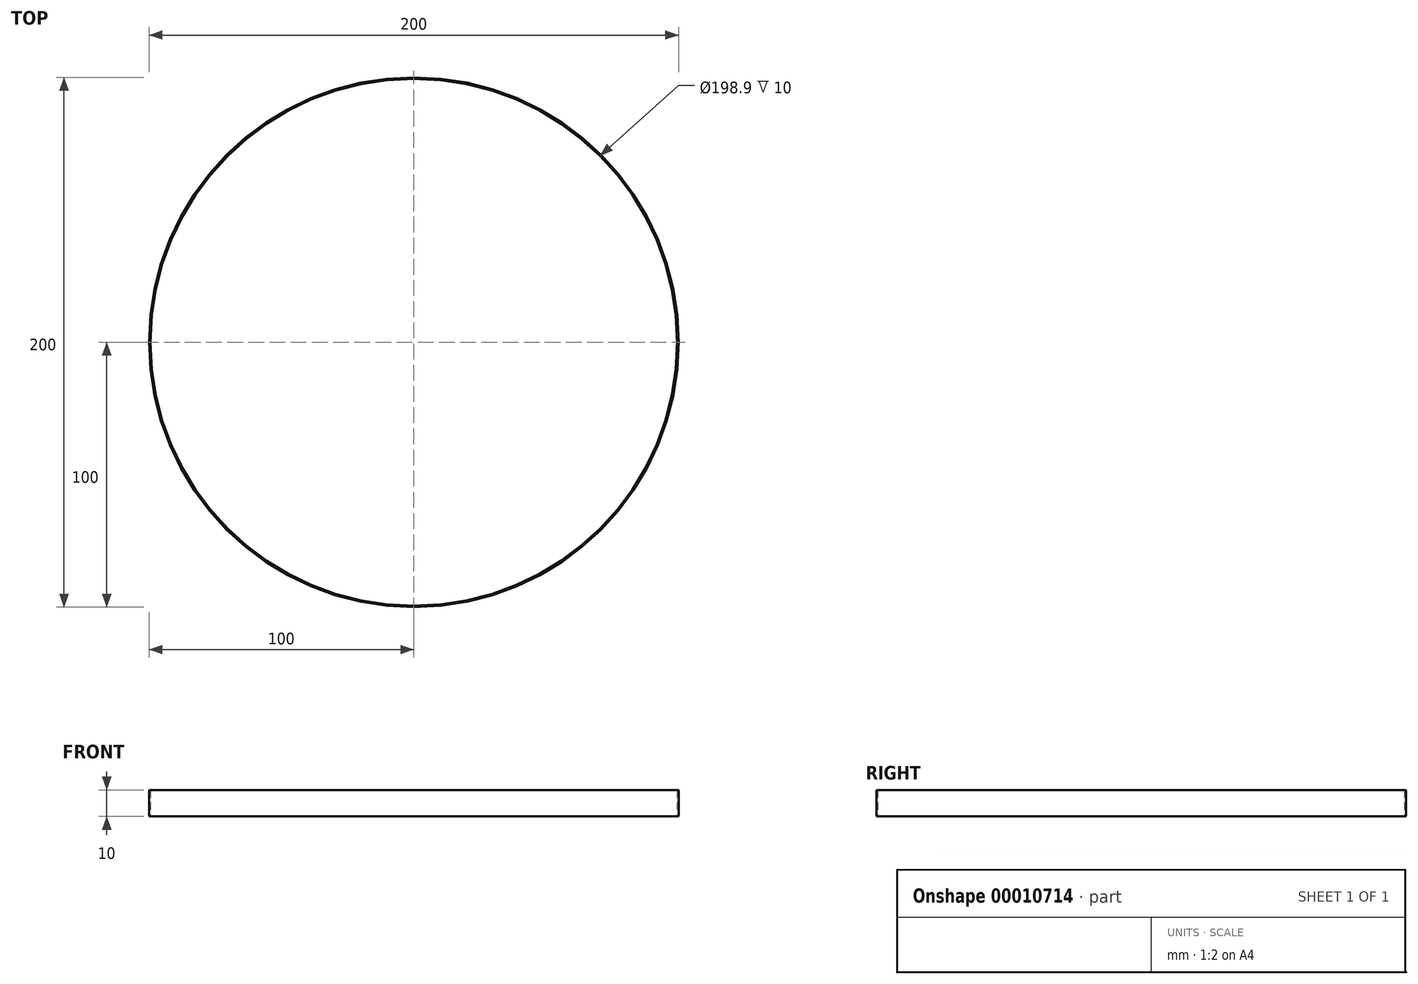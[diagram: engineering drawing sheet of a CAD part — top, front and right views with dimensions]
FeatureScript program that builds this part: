
annotation { "Feature Type Name" : "Feature", "Feature Type Description" : "" }
export const myFeature = defineFeature(function(context is Context, id is Id, definition is map)
    precondition{}
    {
        {
            var Q0;
            Q0=qCreatedBy(makeId("Top.planeOp"),FACE);
            var sketch = newSketch(context, id + "F0", { "sketchPlane" : qUnion([Q0])});
            skCircle(sketch, "E0", {"center": v(0, 0) * mm, "radius": 99.45 * mm});
            skCircle(sketch, "E1", {"center": v(0, 0) * mm, "radius": 100 * mm});
            skSolve(sketch);
        }
        {
            var Q0;
            Q0=makeQuery(id+"F0.imprint","IMPRINT",FACE,{"disambiguationData":[TD([[makeQuery(id+"F0.imprint","IMPRINT",EDGE,{"derivedFrom":sQuery(id+"F0.wireOp",EDGE,"E0")}),-1.0]])]});
            extrude(context, id + "F1", {"entities" : qUnion([Q0]), "depth" : 10 * mm});
        }
    });
